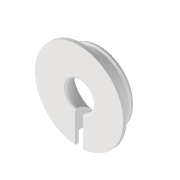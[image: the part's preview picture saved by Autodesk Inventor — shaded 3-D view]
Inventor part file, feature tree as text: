
AUTODESK INVENTOR PART (.ipt)
format: ipt  version: 2021 (Build 250183000, 183)  size: 206,848 bytes
history: native  units: mm
features: extrude x4, fillet x4, sketch x4, chamfer x2, projected_geometry x2
ambient origin geometry x8: Origin, YZ Plane, XZ Plane, XY Plane, X Axis, Y Axis, Z Axis, Center Point
bodies: Volumenkörper1 (feature_tree)
feature tree (16):
  extrude  "Extrusion1"  Depth=1.8mm
  extrude  "Extrusion2"  Depth=3.0mm TaperAngle=0.0deg
  extrude  "Extrusion3"  Depth=1.8mm
  extrude  "Extrusion4"  Depth=0.5mm
  chamfer  "Fase2"  Distance=1.8mm
  fillet  "Rundung5"  Radius=1.4mm
  chamfer  "Fase3"  [1 undecoded]
  fillet  "Rundung6"  Radius=0.3mm
  fillet  "Rundung7"  Radius=6.0mm
  fillet  "Rundung8"  Radius=0.7mm
  sketch  "Skizze1"  dims[d0=14.9mm d1=1.8mm]
  sketch  "Skizze2"  dims[d2=4.5mm d3=3.0mm d4=0.0mm]
  projected_geometry  "Projizierte Kontur1"
  sketch  "Skizze3"  dims[d5=20.0mm d6=1.8mm]
  projected_geometry  "Projizierte Kontur2"
  sketch  "Skizze4"  dims[d7=0.8mm d8=0.0mm d9=15.5mm d10=1.8mm d11=1.4mm d12=0.0mm d20=0.0mm d21=0.0mm d22=0.3mm d23=2.0mm d24=45.0deg d25=6.0mm d26=0.7mm d27=2.0mm d28=45.0deg d29=0.5mm d30=0.2mm d31=0.5mm]
note: 1 required parameter value undecoded (feature->parameter linkage not recoverable at this tier; creation-order binding heuristic only, values carry confidence <= 0.55)
